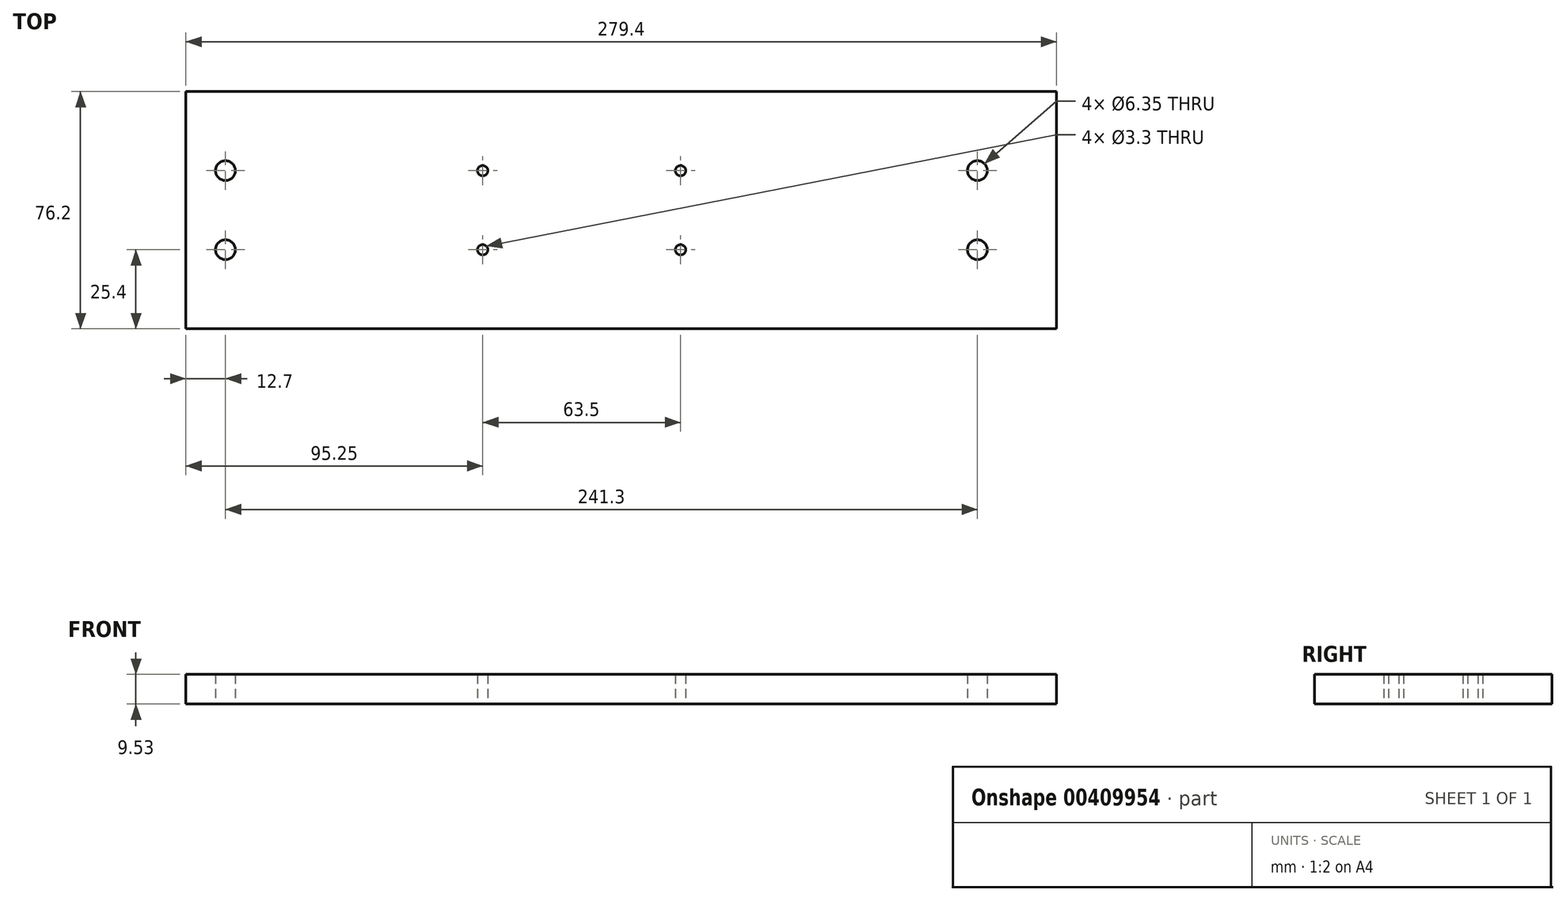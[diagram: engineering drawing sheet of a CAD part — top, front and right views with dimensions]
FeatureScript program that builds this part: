
annotation { "Feature Type Name" : "Feature", "Feature Type Description" : "" }
export const myFeature = defineFeature(function(context is Context, id is Id, definition is map)
    precondition{}
    {
        {
            var Q0;
            Q0=qCreatedBy(makeId("Top.planeOp"),FACE);
            var sketch = newSketch(context, id + "F0", { "sketchPlane" : qUnion([Q0])});
            skLineSegment(sketch, "E0.bottom", {"start": v(127, 38.1) * mm, "end": v(-152.4, 38.1) * mm});
            skLineSegment(sketch, "E0.top", {"start": v(127, -38.1) * mm, "end": v(-152.4, -38.1) * mm});
            skLineSegment(sketch, "E0.left", {"start": v(127, 38.1) * mm, "end": v(127, -38.1) * mm});
            skLineSegment(sketch, "E0.right", {"start": v(-152.4, 38.1) * mm, "end": v(-152.4, -38.1) * mm});
            skPoint(sketch, "E0.middle", {"position": v(0, 0) * mm});
            skPoint(sketch, "E1.endSnap0", {"position": v(-152.4, 0) * mm});
            skSolve(sketch);
        }
        {
            var Q0;
            Q0 = qSketchRegion(id + "F0", true);
            extrude(context, id + "F1", {"entities" : qUnion([Q0]), "depth" : 9.52 * mm});
        }
        {
            var Q0;
            Q0=qCreatedBy(makeId("Top.planeOp"),FACE);
            var sketch = newSketch(context, id + "F2", { "sketchPlane" : qUnion([Q0])});
            skLineSegment(sketch, "E2", {"start": v(140.72, 0) * mm, "end": v(-184.52, 0) * mm, "construction": true});
            skCircle(sketch, "E3", {"center": v(101.6, 12.7) * mm, "radius": 3.18 * mm});
            skCircle(sketch, "E4", {"center": v(6.35, 12.7) * mm, "radius": 1.65 * mm});
            skCircle(sketch, "E5", {"center": v(-57.15, 12.7) * mm, "radius": 1.65 * mm});
            skCircle(sketch, "E6", {"center": v(-139.7, 12.7) * mm, "radius": 3.18 * mm});
            skCircle(sketch, "E7.MirrorC", {"center": v(-139.7, -12.7) * mm, "radius": 3.18 * mm});
            skCircle(sketch, "E8.MirrorC", {"center": v(-57.15, -12.7) * mm, "radius": 1.65 * mm});
            skCircle(sketch, "E9.MirrorC", {"center": v(6.35, -12.7) * mm, "radius": 1.65 * mm});
            skCircle(sketch, "E10.MirrorC", {"center": v(101.6, -12.7) * mm, "radius": 3.18 * mm});
            skSolve(sketch);
        }
        {
            var Q0;
            Q0 = qSketchRegion(id + "F2", true);
            extrude(context, id + "F3", {"entities" : qUnion([Q0]), "operationType" : NewBodyOperationType.REMOVE, "endBound" : BoundingType.THROUGH_ALL, "depth" : 25.4 * mm});
        }
    });
